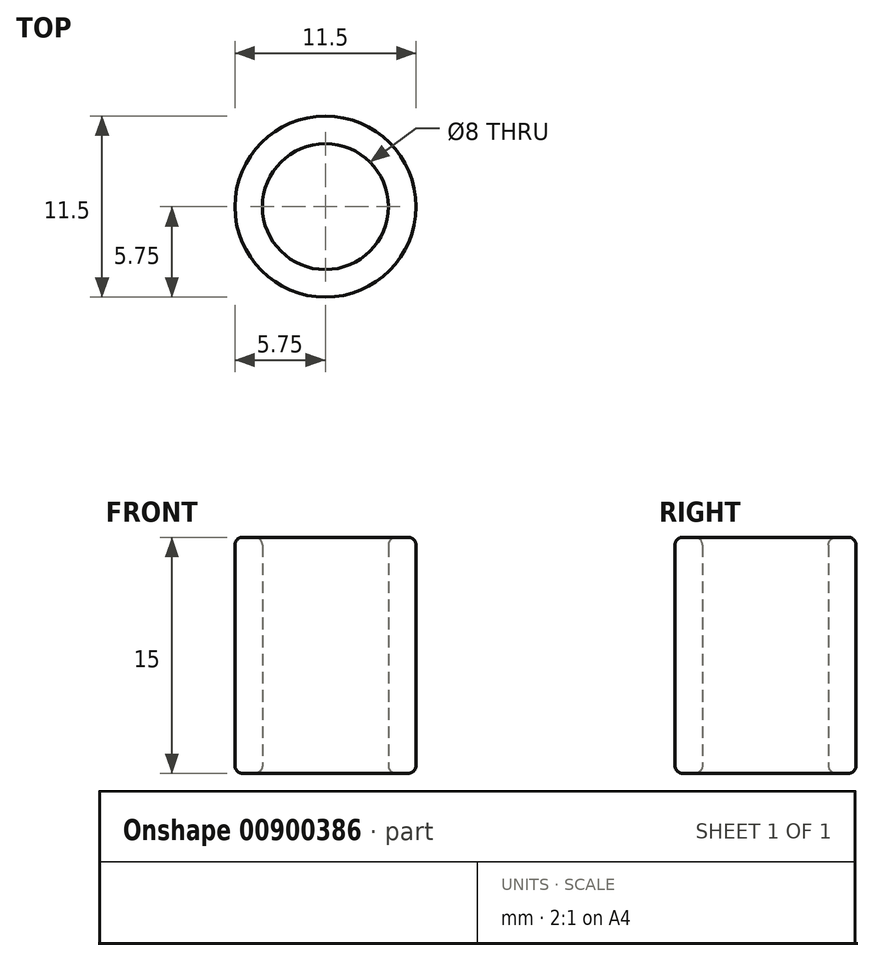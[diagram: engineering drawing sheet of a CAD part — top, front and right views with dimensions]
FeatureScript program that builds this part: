
annotation { "Feature Type Name" : "Feature", "Feature Type Description" : "" }
export const myFeature = defineFeature(function(context is Context, id is Id, definition is map)
    precondition{}
    {
        {
            var Q0;
            Q0=qCreatedBy(makeId("Top.planeOp"),FACE);
            var sketch = newSketch(context, id + "F0", { "sketchPlane" : qUnion([Q0])});
            skCircle(sketch, "E0", {"center": v(0, 0) * mm, "radius": 4 * mm});
            skCircle(sketch, "E1", {"center": v(0, 0) * mm, "radius": 5.75 * mm});
            skSolve(sketch);
        }
        {
            var Q0;
            Q0=makeQuery(id+"F0.imprint","IMPRINT",FACE,{"disambiguationData":[TD([[makeQuery(id+"F0.imprint","IMPRINT",EDGE,{"derivedFrom":sQuery(id+"F0.wireOp",EDGE,"E0")}),-1.0]])]});
            extrude(context, id + "F1", {"entities" : qUnion([Q0]), "depth" : 15 * mm, "offsetDistance" : 25 * mm});
        }
        {
            var Q0;
            Q0=makeQuery(id+"F1.opExtrude","CAP_FACE",FACE,{"disambiguationData":[OSD([sQuery(id+"F0.wireOp",EDGE,"E0"),sQuery(id+"F0.wireOp",EDGE,"E1")])],"isStart":false});
            var Q1;
            Q1=makeQuery(id+"F1.opExtrude","CAP_FACE",FACE,{"disambiguationData":[OSD([sQuery(id+"F0.wireOp",EDGE,"E0"),sQuery(id+"F0.wireOp",EDGE,"E1")])],"isStart":true});
            fillet(context, id + "F2", {"entities" : qUnion([Q0, Q1]), "radius" : .5 * mm, "tangentPropagation" : true, "allowEdgeOverflow" : false});
        }
    });
